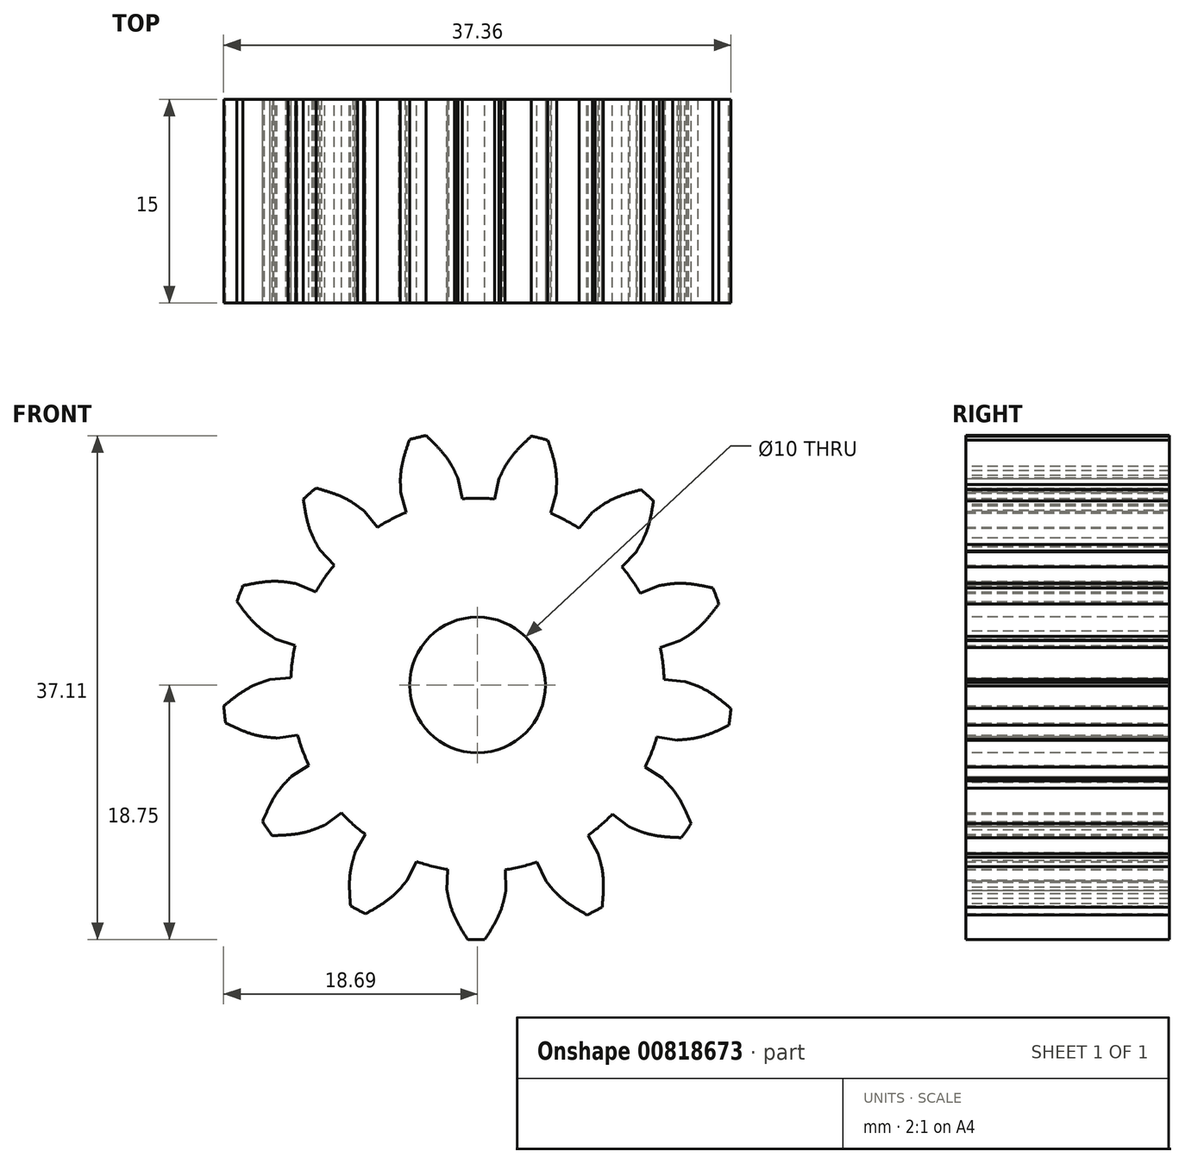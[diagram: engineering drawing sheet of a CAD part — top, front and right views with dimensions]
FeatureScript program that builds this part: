
annotation { "Feature Type Name" : "Feature", "Feature Type Description" : "" }
export const myFeature = defineFeature(function(context is Context, id is Id, definition is map)
    precondition{}
    {
        {
            var Q0;
            Q0=qCreatedBy(makeId("Front.planeOp"),FACE);
            var sketch = newSketch(context, id + "F0", { "sketchPlane" : qUnion([Q0])});
            skCircle(sketch, "E0", {"center": v(0, 0) * mm, "radius": 16.25 * mm, "construction": true});
            skCircle(sketch, "E1", {"center": v(0, 0) * mm, "radius": 18.75 * mm});
            skCircle(sketch, "E2", {"center": v(0, 0) * mm, "radius": 13.75 * mm});
            skCircle(sketch, "E3", {"center": v(0, 0) * mm, "radius": 15.27 * mm, "construction": true});
            skLineSegment(sketch, "E4", {"start": v(-3.93, 16.25) * mm, "end": v(4.33, 16.25) * mm});
            skPoint(sketch, "E5", {"position": v(0, 16.25) * mm});
            skLineSegment(sketch, "E6", {"start": v(5.22, 14.35) * mm, "end": v(-5, 18.07) * mm});
            skLineSegment(sketch, "E7", {"start": v(-5, 18.07) * mm, "end": v(0, 0) * mm, "construction": true});
            skLineSegment(sketch, "E8", {"start": v(0, 0) * mm, "end": v(5.22, 14.35) * mm, "construction": true});
            skPoint(sketch, "E9", {"position": v(-5.66, 14.18) * mm});
            skLineSegment(sketch, "E10", {"start": v(-5.66, 14.18) * mm, "end": v(0, 0) * mm, "construction": true});
            skLineSegment(sketch, "E11", {"start": v(0, 0) * mm, "end": v(2.54, 15.06) * mm, "construction": true});
            skLineSegment(sketch, "E12", {"start": v(0, 0) * mm, "end": v(-0.23, 15.27) * mm, "construction": true});
            skLineSegment(sketch, "E13", {"start": v(0, 0) * mm, "end": v(-3, 14.97) * mm, "construction": true});
            skLineSegment(sketch, "E14", {"start": v(-3, 14.97) * mm, "end": v(-5.66, 14.44) * mm});
            skLineSegment(sketch, "E15", {"start": v(-0.23, 15.27) * mm, "end": v(-5.67, 15.19) * mm});
            skLineSegment(sketch, "E16", {"start": v(2.54, 15.06) * mm, "end": v(-5.51, 16.41) * mm});
            skFitSpline(sketch, "E17", {"points": [v(-5.66, 14.18) * mm, v(-5.66, 14.44) * mm, v(-5.67, 15.19) * mm, v(-5.51, 16.41) * mm, v(-5, 18.07) * mm], "startDerivative": vector(-0.02, 1.7) * mm, "endDerivative": vector(1.68, 4.91) * mm});
            skLineSegment(sketch, "E18", {"start": v(-5.67, 15.19) * mm, "end": v(0, 0) * mm, "construction": true});
            skLineSegment(sketch, "E19", {"start": v(0, 0) * mm, "end": v(-4.4, 18.23) * mm, "construction": true});
            skLineSegment(sketch, "E20", {"start": v(-5.66, 14.18) * mm, "end": v(-5.25, 12.7) * mm});
            skFitSpline(sketch, "E21.MirrorCS", {"points": [v(-1.43, 15.2) * mm, v(-1.54, 15.43) * mm, v(-1.87, 16.1) * mm, v(-2.58, 17.12) * mm, v(-3.78, 18.36) * mm], "startDerivative": vector(-0.76, 1.51) * mm, "endDerivative": vector(-3.73, 3.6) * mm});
            skLineSegment(sketch, "E22.MirrorCS", {"start": v(-1.43, 15.2) * mm, "end": v(-1.12, 13.7) * mm});
            skSolve(sketch);
        }
        {
            var Q0;
            {var subQ1=sQuery(id+"F0.wireOp",EDGE,"E1");var subQ3=sQuery(id+"F0.wireOp",EDGE,"E21.MirrorCS");var subQ4=makeQuery(id+"F0.imprint","INTERSECT",VERTEX,{"derivedFrom":[subQ1,subQ3]});Q0=makeQuery(id+"F0.imprint","IMPRINT",FACE,{"disambiguationData":[TD([[makeQuery(id+"F0.imprint","IMPRINT",EDGE,{"disambiguationData":[TD([[subQ4,1.0]])],"derivedFrom":subQ3}),1.0]])]});}
            var Q1;
            {var subQ0=sQuery(id+"F0.wireOp",EDGE,"E17");var subQ3=sQuery(id+"F0.wireOp",EDGE,"E16");var subQ4=makeQuery(id+"F0.imprint","INTERSECT",VERTEX,{"derivedFrom":[subQ3,subQ0]});Q1=makeQuery(id+"F0.imprint","IMPRINT",FACE,{"disambiguationData":[TD([[makeQuery(id+"F0.imprint","IMPRINT",EDGE,{"disambiguationData":[TD([[subQ4,1.0]])],"derivedFrom":subQ3}),-1.0]])]});}
            var Q2;
            {var subQ0=sQuery(id+"F0.wireOp",EDGE,"E17");var subQ1=sQuery(id+"F0.wireOp",EDGE,"E15");var subQ2=makeQuery(id+"F0.imprint","INTERSECT",VERTEX,{"derivedFrom":[subQ1,subQ0]});Q2=makeQuery(id+"F0.imprint","IMPRINT",FACE,{"disambiguationData":[TD([[makeQuery(id+"F0.imprint","IMPRINT",EDGE,{"disambiguationData":[TD([[subQ2,1.0]])],"derivedFrom":subQ1}),-1.0]])]});}
            var Q3;
            {var subQ4=sQuery(id+"F0.wireOp",EDGE,"E20");Q3=makeQuery(id+"F0.imprint","IMPRINT",FACE,{"disambiguationData":[TD([[makeQuery(id+"F0.imprint","IMPRINT",EDGE,{"derivedFrom":subQ4}),1.0]])]});}
            extrude(context, id + "F1", {"entities" : qUnion([Q0, Q1, Q2, Q3]), "depth" : 15 * mm, "offsetDistance" : 25 * mm});
        }
        {
            var Q0;
            {var subQ0=sQuery(id+"F0.wireOp",EDGE,"E2");var subQ1=makeQuery(id+"F0.imprint","INTERSECT",VERTEX,{"derivedFrom":[subQ0,sQuery(id+"F0.wireOp",EDGE,"E20")]});Q0=makeQuery(id+"F0.imprint","IMPRINT",FACE,{"disambiguationData":[TD([[makeQuery(id+"F0.imprint","IMPRINT",EDGE,{"disambiguationData":[TD([[subQ1,1.0]])],"derivedFrom":subQ0}),1.0]])]});}
            extrude(context, id + "F2", {"entities" : qUnion([Q0]), "depth" : 15 * mm, "offsetDistance" : 25 * mm});
        }
        {
            var Q0;
            Q0=qCreatedBy(makeId("Right.planeOp"),FACE);
            var sketch = newSketch(context, id + "F3", { "sketchPlane" : qUnion([Q0])});
            skLineSegment(sketch, "E23", {"start": v(0, 0) * mm, "end": v(-57.31, 0) * mm});
            skSolve(sketch);
        }
        {
            var Q0;
            Q0=makeQuery(id+"F1.opExtrude","SWEPT_BODY",BODY,{"disambiguationData":[OSD([sQuery(id+"F0.wireOp",EDGE,"E1"),sQuery(id+"F0.wireOp",EDGE,"E2"),sQuery(id+"F0.wireOp",EDGE,"E17"),sQuery(id+"F0.wireOp",EDGE,"E20"),sQuery(id+"F0.wireOp",EDGE,"E21.MirrorCS"),sQuery(id+"F0.wireOp",EDGE,"E22.MirrorCS")])]});
            var Q1;
            Q1=sQuery(id+"F3.wireOp",EDGE,"E23");
            circularPattern(context, id + "F4", {"entities" : qUnion([Q0]), "axis" : qUnion([Q1]), "angle" : 360 * degree, "instanceCount" : 13, "equalSpace" : true});
        }
        {
            var Q0;
            Q0=makeQuery(id+"F4.opPattern","COPY",BODY,{"derivedFrom":makeQuery(id+"F1.opExtrude","SWEPT_BODY",BODY,{"disambiguationData":[OSD([sQuery(id+"F0.wireOp",EDGE,"E1"),sQuery(id+"F0.wireOp",EDGE,"E2"),sQuery(id+"F0.wireOp",EDGE,"E17"),sQuery(id+"F0.wireOp",EDGE,"E20"),sQuery(id+"F0.wireOp",EDGE,"E21.MirrorCS"),sQuery(id+"F0.wireOp",EDGE,"E22.MirrorCS")])]}),"instanceName":"12"});
            var Q1;
            Q1=makeQuery(id+"F1.opExtrude","SWEPT_BODY",BODY,{"disambiguationData":[OSD([sQuery(id+"F0.wireOp",EDGE,"E1"),sQuery(id+"F0.wireOp",EDGE,"E2"),sQuery(id+"F0.wireOp",EDGE,"E17"),sQuery(id+"F0.wireOp",EDGE,"E20"),sQuery(id+"F0.wireOp",EDGE,"E21.MirrorCS"),sQuery(id+"F0.wireOp",EDGE,"E22.MirrorCS")])]});
            var Q2;
            Q2=makeQuery(id+"F2.opExtrude","SWEPT_BODY",BODY,{"disambiguationData":[OSD([sQuery(id+"F0.wireOp",EDGE,"E2")])]});
            var Q3;
            Q3=makeQuery(id+"F4.opPattern","COPY",BODY,{"derivedFrom":makeQuery(id+"F1.opExtrude","SWEPT_BODY",BODY,{"disambiguationData":[OSD([sQuery(id+"F0.wireOp",EDGE,"E1"),sQuery(id+"F0.wireOp",EDGE,"E2"),sQuery(id+"F0.wireOp",EDGE,"E17"),sQuery(id+"F0.wireOp",EDGE,"E20"),sQuery(id+"F0.wireOp",EDGE,"E21.MirrorCS"),sQuery(id+"F0.wireOp",EDGE,"E22.MirrorCS")])]}),"instanceName":"1"});
            var Q4;
            Q4=makeQuery(id+"F4.opPattern","COPY",BODY,{"derivedFrom":makeQuery(id+"F1.opExtrude","SWEPT_BODY",BODY,{"disambiguationData":[OSD([sQuery(id+"F0.wireOp",EDGE,"E1"),sQuery(id+"F0.wireOp",EDGE,"E2"),sQuery(id+"F0.wireOp",EDGE,"E17"),sQuery(id+"F0.wireOp",EDGE,"E20"),sQuery(id+"F0.wireOp",EDGE,"E21.MirrorCS"),sQuery(id+"F0.wireOp",EDGE,"E22.MirrorCS")])]}),"instanceName":"2"});
            var Q5;
            Q5=makeQuery(id+"F4.opPattern","COPY",BODY,{"derivedFrom":makeQuery(id+"F1.opExtrude","SWEPT_BODY",BODY,{"disambiguationData":[OSD([sQuery(id+"F0.wireOp",EDGE,"E1"),sQuery(id+"F0.wireOp",EDGE,"E2"),sQuery(id+"F0.wireOp",EDGE,"E17"),sQuery(id+"F0.wireOp",EDGE,"E20"),sQuery(id+"F0.wireOp",EDGE,"E21.MirrorCS"),sQuery(id+"F0.wireOp",EDGE,"E22.MirrorCS")])]}),"instanceName":"3"});
            var Q6;
            Q6=makeQuery(id+"F4.opPattern","COPY",BODY,{"derivedFrom":makeQuery(id+"F1.opExtrude","SWEPT_BODY",BODY,{"disambiguationData":[OSD([sQuery(id+"F0.wireOp",EDGE,"E1"),sQuery(id+"F0.wireOp",EDGE,"E2"),sQuery(id+"F0.wireOp",EDGE,"E17"),sQuery(id+"F0.wireOp",EDGE,"E20"),sQuery(id+"F0.wireOp",EDGE,"E21.MirrorCS"),sQuery(id+"F0.wireOp",EDGE,"E22.MirrorCS")])]}),"instanceName":"4"});
            var Q7;
            Q7=makeQuery(id+"F4.opPattern","COPY",BODY,{"derivedFrom":makeQuery(id+"F1.opExtrude","SWEPT_BODY",BODY,{"disambiguationData":[OSD([sQuery(id+"F0.wireOp",EDGE,"E1"),sQuery(id+"F0.wireOp",EDGE,"E2"),sQuery(id+"F0.wireOp",EDGE,"E17"),sQuery(id+"F0.wireOp",EDGE,"E20"),sQuery(id+"F0.wireOp",EDGE,"E21.MirrorCS"),sQuery(id+"F0.wireOp",EDGE,"E22.MirrorCS")])]}),"instanceName":"5"});
            var Q8;
            Q8=makeQuery(id+"F4.opPattern","COPY",BODY,{"derivedFrom":makeQuery(id+"F1.opExtrude","SWEPT_BODY",BODY,{"disambiguationData":[OSD([sQuery(id+"F0.wireOp",EDGE,"E1"),sQuery(id+"F0.wireOp",EDGE,"E2"),sQuery(id+"F0.wireOp",EDGE,"E17"),sQuery(id+"F0.wireOp",EDGE,"E20"),sQuery(id+"F0.wireOp",EDGE,"E21.MirrorCS"),sQuery(id+"F0.wireOp",EDGE,"E22.MirrorCS")])]}),"instanceName":"6"});
            var Q9;
            Q9=makeQuery(id+"F4.opPattern","COPY",BODY,{"derivedFrom":makeQuery(id+"F1.opExtrude","SWEPT_BODY",BODY,{"disambiguationData":[OSD([sQuery(id+"F0.wireOp",EDGE,"E1"),sQuery(id+"F0.wireOp",EDGE,"E2"),sQuery(id+"F0.wireOp",EDGE,"E17"),sQuery(id+"F0.wireOp",EDGE,"E20"),sQuery(id+"F0.wireOp",EDGE,"E21.MirrorCS"),sQuery(id+"F0.wireOp",EDGE,"E22.MirrorCS")])]}),"instanceName":"7"});
            var Q10;
            Q10=makeQuery(id+"F4.opPattern","COPY",BODY,{"derivedFrom":makeQuery(id+"F1.opExtrude","SWEPT_BODY",BODY,{"disambiguationData":[OSD([sQuery(id+"F0.wireOp",EDGE,"E1"),sQuery(id+"F0.wireOp",EDGE,"E2"),sQuery(id+"F0.wireOp",EDGE,"E17"),sQuery(id+"F0.wireOp",EDGE,"E20"),sQuery(id+"F0.wireOp",EDGE,"E21.MirrorCS"),sQuery(id+"F0.wireOp",EDGE,"E22.MirrorCS")])]}),"instanceName":"8"});
            var Q11;
            Q11=makeQuery(id+"F4.opPattern","COPY",BODY,{"derivedFrom":makeQuery(id+"F1.opExtrude","SWEPT_BODY",BODY,{"disambiguationData":[OSD([sQuery(id+"F0.wireOp",EDGE,"E1"),sQuery(id+"F0.wireOp",EDGE,"E2"),sQuery(id+"F0.wireOp",EDGE,"E17"),sQuery(id+"F0.wireOp",EDGE,"E20"),sQuery(id+"F0.wireOp",EDGE,"E21.MirrorCS"),sQuery(id+"F0.wireOp",EDGE,"E22.MirrorCS")])]}),"instanceName":"9"});
            var Q12;
            Q12=makeQuery(id+"F4.opPattern","COPY",BODY,{"derivedFrom":makeQuery(id+"F1.opExtrude","SWEPT_BODY",BODY,{"disambiguationData":[OSD([sQuery(id+"F0.wireOp",EDGE,"E1"),sQuery(id+"F0.wireOp",EDGE,"E2"),sQuery(id+"F0.wireOp",EDGE,"E17"),sQuery(id+"F0.wireOp",EDGE,"E20"),sQuery(id+"F0.wireOp",EDGE,"E21.MirrorCS"),sQuery(id+"F0.wireOp",EDGE,"E22.MirrorCS")])]}),"instanceName":"10"});
            var Q13;
            Q13=makeQuery(id+"F4.opPattern","COPY",BODY,{"derivedFrom":makeQuery(id+"F1.opExtrude","SWEPT_BODY",BODY,{"disambiguationData":[OSD([sQuery(id+"F0.wireOp",EDGE,"E1"),sQuery(id+"F0.wireOp",EDGE,"E2"),sQuery(id+"F0.wireOp",EDGE,"E17"),sQuery(id+"F0.wireOp",EDGE,"E20"),sQuery(id+"F0.wireOp",EDGE,"E21.MirrorCS"),sQuery(id+"F0.wireOp",EDGE,"E22.MirrorCS")])]}),"instanceName":"11"});
            booleanBodies(context, id + "F5", {"operationType" : BooleanOperationType.UNION, "tools" : qUnion([Q0, Q1, Q2, Q3, Q4, Q5, Q6, Q7, Q8, Q9, Q10, Q11, Q12, Q13])});
        }
        {
            var Q0;
            {var subQ0=sQuery(id+"F0.wireOp",EDGE,"E2");var subQ1=makeQuery(id+"F1.opExtrude","CAP_FACE",FACE,{"disambiguationData":[OSD([sQuery(id+"F0.wireOp",EDGE,"E1"),subQ0,sQuery(id+"F0.wireOp",EDGE,"E17"),sQuery(id+"F0.wireOp",EDGE,"E20"),sQuery(id+"F0.wireOp",EDGE,"E21.MirrorCS"),sQuery(id+"F0.wireOp",EDGE,"E22.MirrorCS")])],"isStart":false});Q0=makeQuery(id+"F5.opBoolean","MERGE",FACE,{"derivedFrom":[subQ1,makeQuery(id+"F2.opExtrude","CAP_FACE",FACE,{"disambiguationData":[OSD([subQ0])],"isStart":false}),makeQuery(id+"F4.opPattern","COPY",FACE,{"derivedFrom":subQ1,"instanceName":"1"}),makeQuery(id+"F4.opPattern","COPY",FACE,{"derivedFrom":subQ1,"instanceName":"2"}),makeQuery(id+"F4.opPattern","COPY",FACE,{"derivedFrom":subQ1,"instanceName":"3"}),makeQuery(id+"F4.opPattern","COPY",FACE,{"derivedFrom":subQ1,"instanceName":"4"}),makeQuery(id+"F4.opPattern","COPY",FACE,{"derivedFrom":subQ1,"instanceName":"5"}),makeQuery(id+"F4.opPattern","COPY",FACE,{"derivedFrom":subQ1,"instanceName":"6"}),makeQuery(id+"F4.opPattern","COPY",FACE,{"derivedFrom":subQ1,"instanceName":"7"}),makeQuery(id+"F4.opPattern","COPY",FACE,{"derivedFrom":subQ1,"instanceName":"8"}),makeQuery(id+"F4.opPattern","COPY",FACE,{"derivedFrom":subQ1,"instanceName":"9"}),makeQuery(id+"F4.opPattern","COPY",FACE,{"derivedFrom":subQ1,"instanceName":"10"}),makeQuery(id+"F4.opPattern","COPY",FACE,{"derivedFrom":subQ1,"instanceName":"11"}),makeQuery(id+"F4.opPattern","COPY",FACE,{"derivedFrom":subQ1,"instanceName":"12"})]});}
            var sketch = newSketch(context, id + "F6", { "sketchPlane" : qUnion([Q0])});
            skCircle(sketch, "E24", {"center": v(0, 0) * mm, "radius": 5 * mm});
            skSolve(sketch);
        }
        {
            var Q0;
            Q0 = qSketchRegion(id + "F6", true);
            extrude(context, id + "F7", {"entities" : qUnion([Q0]), "operationType" : NewBodyOperationType.REMOVE, "endBound" : BoundingType.THROUGH_ALL, "oppositeDirection" : true, "depth" : 25 * mm, "offsetDistance" : 25 * mm});
        }
    });
